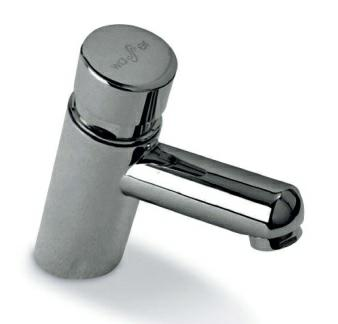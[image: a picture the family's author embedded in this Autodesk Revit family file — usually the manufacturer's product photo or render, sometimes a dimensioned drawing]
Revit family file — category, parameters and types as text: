
# Revit family: CW2010001
name_source: partatom
category: Aparatos sanitarios
revit_build: Autodesk Revit 2016 (Build: 20150220_1215(x64)
units: mm (PartAtom-declared; Revit-internal decimal feet)

## family parameters
Compartido = No
Corte con vacíos al cargar = No
Cota de conector redondo = Diámetro de uso
Número OmniClass = 23.45.00.00
Punto de cálculo de habitación = No
Se basa en plano de trabajo = No
Siempre vertical = Sí
Tipo de pieza = Normal
Título OmniClass = Sanitary, Laundry, and Cleaning Equipment

## types (1)
- 135 x 119
    Conexión AC = No
    Conexión AF = Sí
    Conexión de residuos = No
    Conexión de ventilación = No
    Código de montaje = D2010
    Descripción = Grifo temporizado inclinado para lavabo 1/2"
    Fabricante = CHC
    Height = 800 mm  [stored 2.62467 ft]
    Imagen de tipo = CW8002001.jpg
    Material = Stainless Steel, Polished
    Modelo = CW8002001
    URL = www.grupochc.cl

note: [stored X ft] marks values corroborated as IEEE doubles in the binary element streams (Revit-internal decimal feet)

## geometry (parser evidence)
native form markers: Sweep x2
no freeform markers — native parametric forms only
